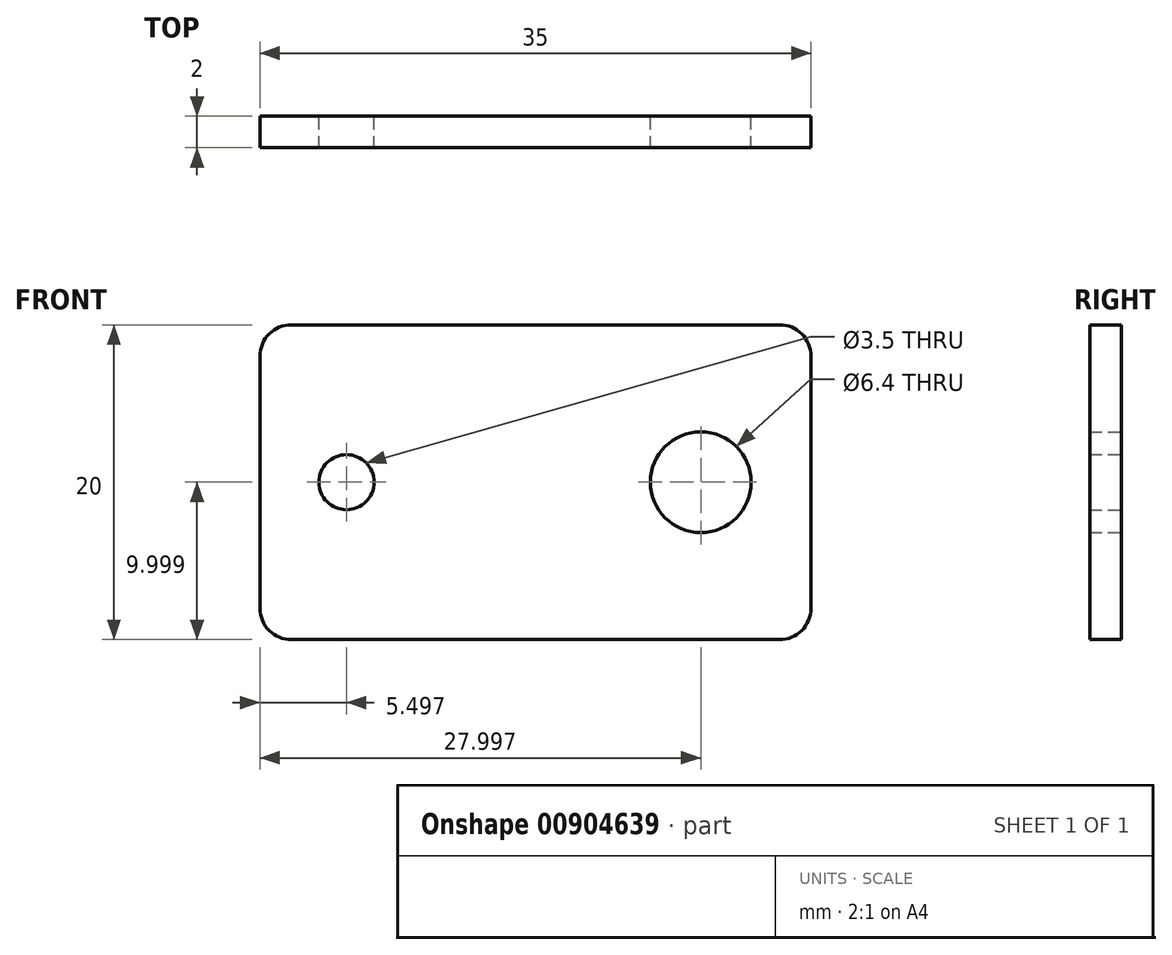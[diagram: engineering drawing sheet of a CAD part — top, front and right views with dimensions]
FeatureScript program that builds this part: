
annotation { "Feature Type Name" : "Feature", "Feature Type Description" : "" }
export const myFeature = defineFeature(function(context is Context, id is Id, definition is map)
    precondition{}
    {
        {
            var Q0;
            Q0=qCreatedBy(makeId("Front.planeOp"),FACE);
            var sketch = newSketch(context, id + "F0", { "sketchPlane" : qUnion([Q0])});
            skLineSegment(sketch, "E0.bottom", {"start": v(-33.65, 27.67) * mm, "end": v(-2.65, 27.67) * mm});
            skLineSegment(sketch, "E0.top", {"start": v(-33.65, 7.67) * mm, "end": v(-2.65, 7.67) * mm});
            skLineSegment(sketch, "E0.left", {"start": v(-35.65, 25.67) * mm, "end": v(-35.65, 9.67) * mm});
            skLineSegment(sketch, "E0.right", {"start": v(-0.65, 25.67) * mm, "end": v(-0.65, 9.67) * mm});
            skLineSegment(sketch, "E1", {"start": v(-35.65, 17.67) * mm, "end": v(32.68, 17.67) * mm, "construction": true});
            skCircle(sketch, "E2", {"center": v(-30.15, 17.67) * mm, "radius": 1.75 * mm});
            skCircle(sketch, "E3", {"center": v(-7.65, 17.67) * mm, "radius": 3.2 * mm});
            skPoint(sketch, "E4.visualSharp", {"position": v(-35.65, 27.67) * mm});
            skArc(sketch, "E4.filletArc", {"start": v(-33.65, 27.67) * mm, "mid": v(-35.07, 27.08) * mm, "end": v(-35.65, 25.67) * mm});
            skPoint(sketch, "E5.visualSharp", {"position": v(-0.65, 27.67) * mm});
            skArc(sketch, "E5.filletArc", {"start": v(-0.65, 25.67) * mm, "mid": v(-1.24, 27.08) * mm, "end": v(-2.65, 27.67) * mm});
            skPoint(sketch, "E6.visualSharp", {"position": v(-0.65, 7.67) * mm});
            skArc(sketch, "E6.filletArc", {"start": v(-2.65, 7.67) * mm, "mid": v(-1.24, 8.26) * mm, "end": v(-0.65, 9.67) * mm});
            skPoint(sketch, "E7.visualSharp", {"position": v(-35.65, 7.67) * mm});
            skArc(sketch, "E7.filletArc", {"start": v(-35.65, 9.67) * mm, "mid": v(-35.07, 8.26) * mm, "end": v(-33.65, 7.67) * mm});
            skSolve(sketch);
        }
        {
            var Q0;
            Q0=makeQuery(id+"F0.imprint","IMPRINT",FACE,{"disambiguationData":[TD([[makeQuery(id+"F0.imprint","IMPRINT",EDGE,{"derivedFrom":sQuery(id+"F0.wireOp",EDGE,"E0.bottom")}),-1.0]])]});
            extrude(context, id + "F1", {"entities" : qUnion([Q0]), "depth" : 2 * mm, "offsetDistance" : 25 * mm});
        }
    });
